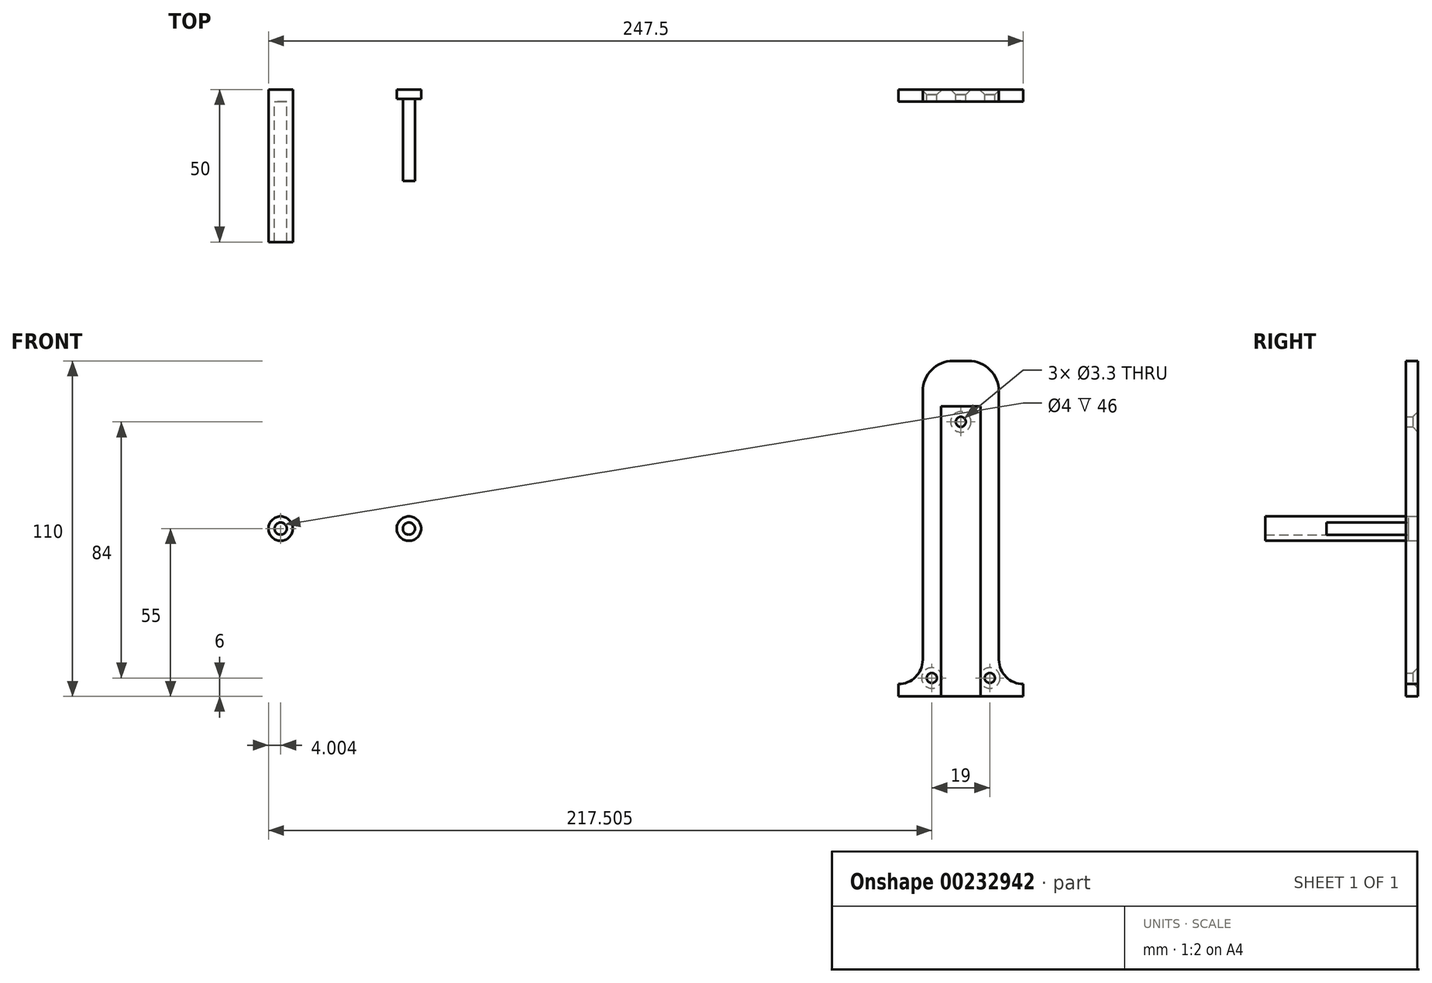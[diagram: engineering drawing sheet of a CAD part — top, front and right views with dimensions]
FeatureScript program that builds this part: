
annotation { "Feature Type Name" : "Feature", "Feature Type Description" : "" }
export const myFeature = defineFeature(function(context is Context, id is Id, definition is map)
    precondition{}
    {
        {
            var Q0;
            Q0=qCreatedBy(makeId("Front.planeOp"),FACE);
            var sketch = newSketch(context, id + "F0", { "sketchPlane" : qUnion([Q0])});
            skCircle(sketch, "E0", {"center": v(0, 0) * mm, "radius": 4 * mm});
            skCircle(sketch, "E1", {"center": v(0, 0) * mm, "radius": 2 * mm});
            skLineSegment(sketch, "E2", {"start": v(-21.03, 0) * mm, "end": v(-21.03, 14.12) * mm});
            skCircle(sketch, "E3.MirrorC", {"center": v(-42.06, 0) * mm, "radius": 2 * mm});
            skCircle(sketch, "E4.MirrorC", {"center": v(-42.06, 0) * mm, "radius": 4 * mm});
            skSolve(sketch);
        }
        {
            var Q0;
            Q0=makeQuery(id+"F0.imprint","IMPRINT",FACE,{"disambiguationData":[TD([[makeQuery(id+"F0.imprint","IMPRINT",EDGE,{"derivedFrom":sQuery(id+"F0.wireOp",EDGE,"E1")}),1.0]])]});
            extrude(context, id + "F1", {"entities" : qUnion([Q0]), "depth" : 80 * mm});
        }
        {
            var Q0;
            Q0=makeQuery(id+"F0.imprint","IMPRINT",FACE,{"disambiguationData":[TD([[makeQuery(id+"F0.imprint","IMPRINT",EDGE,{"derivedFrom":sQuery(id+"F0.wireOp",EDGE,"E0")}),1.0]])]});
            extrude(context, id + "F2", {"entities" : qUnion([Q0]), "operationType" : NewBodyOperationType.ADD, "depth" : 3 * mm});
        }
        {
            var Q0;
            Q0=makeQuery(id+"F1.opExtrude","CAP_FACE",FACE,{"disambiguationData":[OSD([sQuery(id+"F0.wireOp",EDGE,"E1")])],"isStart":false});
            extrude(context, id + "F3", {"entities" : qUnion([Q0]), "operationType" : NewBodyOperationType.REMOVE, "oppositeDirection" : true, "depth" : 50 * mm});
        }
        {
            var Q0;
            Q0=qCreatedBy(makeId("Front.planeOp"),FACE);
            var sketch = newSketch(context, id + "F4", { "sketchPlane" : qUnion([Q0])});
            skLineSegment(sketch, "E5.bottom", {"start": v(168.44, -55) * mm, "end": v(193.44, -55) * mm});
            skLineSegment(sketch, "E5.top", {"start": v(178.44, 55) * mm, "end": v(183.44, 55) * mm});
            skLineSegment(sketch, "E5.left", {"start": v(168.44, -43) * mm, "end": v(168.44, 45) * mm});
            skLineSegment(sketch, "E5.right", {"start": v(193.44, -43) * mm, "end": v(193.44, 45) * mm});
            skPoint(sketch, "E5.middle", {"position": v(180.94, 0) * mm});
            skLineSegment(sketch, "E6", {"start": v(180.94, 0) * mm, "end": v(180.94, 35) * mm});
            skLineSegment(sketch, "E7.top", {"start": v(174.44, 40.07) * mm, "end": v(187.44, 40.07) * mm});
            skLineSegment(sketch, "E7.left", {"start": v(174.44, 29.93) * mm, "end": v(174.44, 40.07) * mm});
            skLineSegment(sketch, "E7.right", {"start": v(187.44, 29.93) * mm, "end": v(187.44, 40.07) * mm});
            skPoint(sketch, "E7.middle", {"position": v(180.94, 35) * mm});
            skLineSegment(sketch, "E8", {"start": v(174.44, 29.93) * mm, "end": v(174.44, -55) * mm});
            skLineSegment(sketch, "E9", {"start": v(187.44, 29.93) * mm, "end": v(187.44, -55) * mm});
            skPoint(sketch, "E10.visualSharp", {"position": v(168.44, 55) * mm});
            skArc(sketch, "E10.filletArc", {"start": v(178.44, 55) * mm, "mid": v(171.37, 52.07) * mm, "end": v(168.44, 45) * mm});
            skPoint(sketch, "E11.visualSharp", {"position": v(193.44, 55) * mm});
            skArc(sketch, "E11.filletArc", {"start": v(193.44, 45) * mm, "mid": v(190.52, 52.07) * mm, "end": v(183.44, 55) * mm});
            skLineSegment(sketch, "E12", {"start": v(168.44, -55) * mm, "end": v(160.44, -55) * mm});
            skLineSegment(sketch, "E13", {"start": v(180.94, -55) * mm, "end": v(180.94, -28.74) * mm});
            skLineSegment(sketch, "E14", {"start": v(168.44, -43) * mm, "end": v(169.34, -43) * mm});
            skLineSegment(sketch, "E15", {"start": v(160.44, -55) * mm, "end": v(160.44, -51) * mm});
            skArc(sketch, "E16", {"start": v(160.44, -51) * mm, "mid": v(166.1, -48.66) * mm, "end": v(168.44, -43) * mm});
            skArc(sketch, "E17.MirrorCS", {"start": v(201.44, -51) * mm, "mid": v(195.79, -48.66) * mm, "end": v(193.44, -43) * mm});
            skLineSegment(sketch, "E18.MirrorCS", {"start": v(201.44, -55) * mm, "end": v(201.44, -51) * mm});
            skLineSegment(sketch, "E19.MirrorCS", {"start": v(193.44, -55) * mm, "end": v(201.44, -55) * mm});
            skPoint(sketch, "E20", {"position": v(171.44, -49) * mm});
            skPoint(sketch, "E21.MirrorP", {"position": v(190.44, -49) * mm});
            skSolve(sketch);
        }
        {
            var Q0;
            Q0=makeQuery(id+"F4.imprint","IMPRINT",FACE,{"disambiguationData":[TD([[makeQuery(id+"F4.imprint","IMPRINT",EDGE,{"derivedFrom":sQuery(id+"F4.wireOp",EDGE,"E5.top")}),-1.0]])]});
            var Q1;
            Q1=makeQuery(id+"F0.imprint","IMPRINT",FACE,{"disambiguationData":[TD([[makeQuery(id+"F0.imprint","IMPRINT",EDGE,{"derivedFrom":sQuery(id+"F0.wireOp",EDGE,"E3.MirrorC")}),1.0]])]});
            extrude(context, id + "F5", {"entities" : qUnion([Q0, Q1]), "depth" : 4 * mm});
        }
        {
            var Q0;
            Q0=makeQuery(id+"F4.imprint","IMPRINT",FACE,{"disambiguationData":[TD([[makeQuery(id+"F4.imprint","IMPRINT",EDGE,{"derivedFrom":sQuery(id+"F4.wireOp",EDGE,"E7.top")}),-1.0]])]});
            extrude(context, id + "F6", {"entities" : qUnion([Q0]), "operationType" : NewBodyOperationType.ADD, "depth" : 3.7 * mm});
        }
        {
            var Q0;
            Q0=sQuery(id+"F4.wireOp",VERTEX,"E7.middle");
            var Q1;
            Q1=makeQuery(id+"F5.opExtrude","SWEPT_BODY",BODY,{"disambiguationData":[OSD([sQuery(id+"F4.wireOp",EDGE,"E5.bottom"),sQuery(id+"F4.wireOp",EDGE,"E5.top"),sQuery(id+"F4.wireOp",EDGE,"E5.left"),sQuery(id+"F4.wireOp",EDGE,"E5.right"),sQuery(id+"F4.wireOp",EDGE,"E7.top"),sQuery(id+"F4.wireOp",EDGE,"E7.left"),sQuery(id+"F4.wireOp",EDGE,"E7.right"),sQuery(id+"F4.wireOp",EDGE,"E8"),sQuery(id+"F4.wireOp",EDGE,"E9"),sQuery(id+"F4.wireOp",EDGE,"E10.filletArc"),sQuery(id+"F4.wireOp",EDGE,"E11.filletArc"),sQuery(id+"F4.wireOp",EDGE,"E12"),sQuery(id+"F4.wireOp",EDGE,"E15"),sQuery(id+"F4.wireOp",EDGE,"E16"),sQuery(id+"F4.wireOp",EDGE,"E17.MirrorCS"),sQuery(id+"F4.wireOp",EDGE,"E18.MirrorCS"),sQuery(id+"F4.wireOp",EDGE,"E19.MirrorCS")])]});
            hole(context, id + "F7", {"style" : HoleStyle.C_SINK, "endStyle" : HoleEndStyle.THROUGH, "oppositeDirection" : true, "standardTappedOrClearance" : lookupTablePath({ "standard" : "ISO", "fit" : "Normal", "size" : "M3", "type" : "Clearance" }), "standardBlindInLast" : lookupTablePath({ "fit" : "Standard", "standard" : "ISO", "size" : "M3", "type" : "Clearance" }), "holeDiameter" : 3.3 * mm, "cSinkDiameter" : 6.72 * mm, "cSinkAngle" : 90 * degree, "locations" : qUnion([Q0]), "scope" : qUnion([Q1]), "isTappedThrough" : true});
        }
        {
            var Q0;
            Q0=sQuery(id+"F4.wireOp",VERTEX,"E21.MirrorP");
            var Q1;
            Q1=sQuery(id+"F4.wireOp",VERTEX,"E20");
            var Q2;
            Q2=makeQuery(id+"F5.opExtrude","SWEPT_BODY",BODY,{"disambiguationData":[OSD([sQuery(id+"F4.wireOp",EDGE,"E5.bottom"),sQuery(id+"F4.wireOp",EDGE,"E5.top"),sQuery(id+"F4.wireOp",EDGE,"E5.left"),sQuery(id+"F4.wireOp",EDGE,"E5.right"),sQuery(id+"F4.wireOp",EDGE,"E7.top"),sQuery(id+"F4.wireOp",EDGE,"E7.left"),sQuery(id+"F4.wireOp",EDGE,"E7.right"),sQuery(id+"F4.wireOp",EDGE,"E8"),sQuery(id+"F4.wireOp",EDGE,"E9"),sQuery(id+"F4.wireOp",EDGE,"E10.filletArc"),sQuery(id+"F4.wireOp",EDGE,"E11.filletArc"),sQuery(id+"F4.wireOp",EDGE,"E12"),sQuery(id+"F4.wireOp",EDGE,"E15"),sQuery(id+"F4.wireOp",EDGE,"E16"),sQuery(id+"F4.wireOp",EDGE,"E17.MirrorCS"),sQuery(id+"F4.wireOp",EDGE,"E18.MirrorCS"),sQuery(id+"F4.wireOp",EDGE,"E19.MirrorCS")])]});
            hole(context, id + "F8", {"style" : HoleStyle.C_SINK, "endStyle" : HoleEndStyle.THROUGH, "oppositeDirection" : true, "standardTappedOrClearance" : lookupTablePath({ "standard" : "ISO", "fit" : "Normal", "size" : "M3", "type" : "Clearance" }), "standardBlindInLast" : lookupTablePath({ "fit" : "Standard", "standard" : "ISO", "size" : "M3", "type" : "Clearance" }), "holeDiameter" : 3.3 * mm, "cSinkDiameter" : 6.72 * mm, "cSinkAngle" : 90 * degree, "locations" : qUnion([Q0, Q1]), "scope" : qUnion([Q2]), "isTappedThrough" : true});
        }
        {
            var Q0;
            Q0=makeQuery(id+"F0.imprint","IMPRINT",FACE,{"disambiguationData":[TD([[makeQuery(id+"F0.imprint","IMPRINT",EDGE,{"derivedFrom":sQuery(id+"F0.wireOp",EDGE,"E3.MirrorC")}),-1.0]])]});
            extrude(context, id + "F9", {"entities" : qUnion([Q0]), "operationType" : NewBodyOperationType.ADD, "depth" : 50 * mm});
        }
    });
